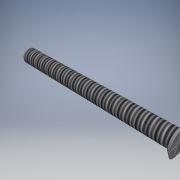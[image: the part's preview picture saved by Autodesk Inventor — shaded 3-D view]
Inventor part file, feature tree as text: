
AUTODESK INVENTOR PART (.ipt)
format: ipt  version: 2016 (Build 200138000, 138)  size: 128,000 bytes
history: native  units: in
note: dims shown in document units (in); Inventor stores cm internally (conversion verified against a paired STEP export)
features: extrude x3, sketch x3, thread x2, chamfer x1
ambient origin geometry x8: Origin, YZ Plane, XZ Plane, XY Plane, X Axis, Y Axis, Z Axis, Center Point
bodies: Solid1 (feature_tree)
feature tree (9):
  extrude  "Extrusion1"  Depth=2.5in TaperAngle=0.0deg
  extrude  "Extrusion2"  Depth=0.05in TaperAngle=0.0deg
  chamfer  "Chamfer1"  Distance=0.05in Angle=45.0deg
  extrude  "Extrusion3"  Depth=0.02in
  thread  "Thread1"  [1 undecoded]
  thread  "Thread2"  [1 undecoded]
  sketch  "Sketch1"  dims[d0=0.25in d1=2.5in d2=0.0in]
  sketch  "Sketch2"  dims[d3=0.4in d4=0.05in d5=0.0in d6=0.05in d7=0.125in d8=45.0deg]
  sketch  "Sketch3"  dims[d9=0.02in d10=0.4in d11=0.4in d12=0.02in d13=0.02in d14=0.0in d15=1.0in d16=0.0in d17=1.0in d18=0.0in]
note: 2 required parameter values undecoded (feature->parameter linkage not recoverable at this tier; creation-order binding heuristic only, values carry confidence <= 0.55)
